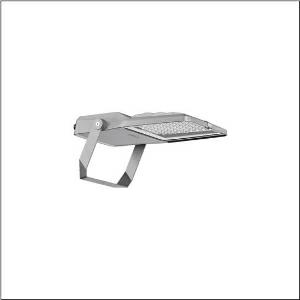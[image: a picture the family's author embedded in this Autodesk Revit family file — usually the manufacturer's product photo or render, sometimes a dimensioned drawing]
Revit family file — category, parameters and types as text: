
# Revit family: floodlight_fl_21_iq_mini___pl43_5xa7771b4a1a_3306
name_source: partatom
category: Lighting Fixtures
units: mm (PartAtom-declared; Revit-internal decimal feet)

## family parameters
Cut with Voids When Loaded = No
Host = Face
Light Source = No
Part Type = Normal
Room Calculation Point = No
Round Connector Dimension = Use Diameter
Shared = No

## types (1)
- --- (1 x LED, 6660 lm, 45.5 W, 4000K)
    Apparent Load = 46 VA
    CIE Flux Codes = 27 78 99 100 100
    Color Rendering = 70
    Color Temperature = 4000K
    Default Elevation = 1800 mm
    Description = Floodlight FL 21 iQ mini, floodlight, primary light control with lens, of PMMA, primary optical cover: protective disc, of toughened safety glass, transparent, light distribution: PL43, light emission: direct distribution, installation type: surface-mounted, LED, High Power LED, rated luminous flux: 6.660lm, luminous efficacy: 146lm/W, light colour: 740, colour temperature: 4000K, control gear: iQ Comfort/DALI, control: Auto-Match, Temp-Guard, Lumen-Switch, Night-Set, Smart-Wire, Light-Fading, Desk-Remote (wireless, voltage-free reading and setting of iQ features in the workshop via application-optimized NFC function/RFID function), optimised constant luminous flux control (CLO 2.0), with terminal, 6-pole, mains connection: 220..240V, AC, 50/60Hz, start of lifetime: 46W, end of service life: 48W, reduction: 22W, luminaire housing, of diecast aluminium, powder-coated, Siteco® metallic grey (DB 702S), corrosivity category C5 mid according to DIN EN ISO 12944, suitable for swimming pools, chlorine-resistant, sealing non-destructively replaceable, mounting bracket, of steel, galvanised, powder-coated, Siteco® metallic grey (DB 702S), protection rating (complete): IP66, insulation class (complete): insulation class II (safety insulation), certification: CE, ENEC, VDE, protection symbol: D, impact resistance: IK08, permissible operating ambient temperature: -40..+40°C, permissible operating ambient temperature for outdoor applications: -40..+50°C, standard: DIN EN 12944, LABS conformity tested according to VDMA 24364:2018-05, packaging unit: 1 piece

Light Distribution: PL43
    Height = 70 mm
    Lamp = 1 x LED
    Lamp Light Flux = 6660 lm
    Lamp Power = 45.5 W
    Lamp count = 1
    Length = 485 mm
    Luminous efficacy = 146 lm/W
    Manufacturer = Siteco
    ModVariant = No
    Model = 5XA7771B4A1A
    Mounting Place = Wall
    Mounting Type = Surface mounted
    Number of Poles = 1
    OnlyDefault = Yes
    Power Factor = 1
    Product Name = Floodlight FL 21 iQ mini | PL43
    Product group = floodlight | wall mounted
    ProductGroupID = 2001
    Protection Class = Protection class II
    Protection Degree = IP 66
    RLX_Detail_Level = 1
    RLX_Emergency_Light_Flux = 0 lm
    RLX_Emergency_Type = 0
    RLX_Emergency_Type_DB = No
    RlxData = <blob elided: 96077 chars, md5=0dc10911>
    Socket = socket
    Standby Power = 0 W
    System Light Flux = 6660 lm
    System Power = 46 W
    Type Comments = factory setting: luminous flux: 100 % | dim-lin: 254 | 463 mA
    Type Image = l_1006845.jpg
    URL = http://relux.com
    VarID = @adj_162014
    Voltage = 0 V
    Weight = 0.00 kg
    Width = 337 mm

## geometry (parser evidence)
native form markers: Blend x4, Sweep x12
no freeform markers — native parametric forms only
